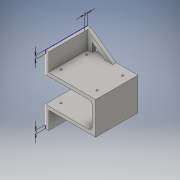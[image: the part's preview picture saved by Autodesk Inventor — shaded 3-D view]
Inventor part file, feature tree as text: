
AUTODESK INVENTOR PART (.ipt)
format: ipt  version: 2016 (Build 200138000, 138)  size: 228,352 bytes
history: native  units: in
note: dims shown in document units (in); Inventor stores cm internally (conversion verified against a paired STEP export)
features: sketch x10, extrude x6, plane x3, hole x1, fillet x1, rib x1
ambient origin geometry x8: Origin, YZ Plane, XZ Plane, XY Plane, X Axis, Y Axis, Z Axis, Center Point
bodies: Solid1 (feature_tree)
feature tree (22):
  extrude  "Extrusion1"  Depth=1.4488in
  extrude  "Extrusion2"  Depth=0.1181in
  sketch  "Sketch3"  dims[d6=0.1181in d7=0.8819in d8=0.0in]
  plane  "Work Plane1"
  extrude  "Extrusion3"  Depth=0.1181in TaperAngle=0.0deg
  hole  "Hole1"  [1 undecoded]
  extrude  "Extrusion4"  Depth=0.128in
  sketch  "Sketch8"  dims[d16=0.128in d17=0.128in d19=0.128in]
  plane  "Work Plane2"
  extrude  "Extrusion5"  Depth=0.128in
  extrude  "Extrusion6"  Depth=0.128in
  fillet  "Fillet1"  Radius=0.128in
  plane  "Work Plane3"
  rib  "Rib1"
  sketch  "Sketch11"  dims[d22=0.0591in d23=0.2362in d24=0.1575in d25=0.0787in d26=90.0deg d27=0.315in d28=0.8108in d29=0.1181in d30=0.0in d31=0.6102in d32=0.0in d33=0.6102in d34=0.0in d35=0.1181in d36=0.1181in d37=0.126in d38=0.8661in d39=0.8661in d40=0.1575in d41=0.1181in d42=0.0in d43=0.0in d44=0.0394in d45=0.0394in d46=0.1181in d49=0.1181in d50=0.1181in]
  sketch  "Sketch1"  dims[d0=1.6102in d1=1.4488in]
  sketch  "Sketch2"  dims[d2=0.1181in d3=0.0in d5=0.1181in]
  sketch  "Sketch5"  dims[d9=0.1181in d10=0.0in d11=1.4921in]
  sketch  "Sketch6"  dims[d12=1.1339in d13=0.128in]
  sketch  "Sketch7"  dims[d14=0.128in d15=0.128in]
  sketch  "Sketch9"  dims[d20=0.128in]
  sketch  "Sketch10"  dims[d21=0.128in]
note: 1 required parameter value undecoded (feature->parameter linkage not recoverable at this tier; creation-order binding heuristic only, values carry confidence <= 0.55)
